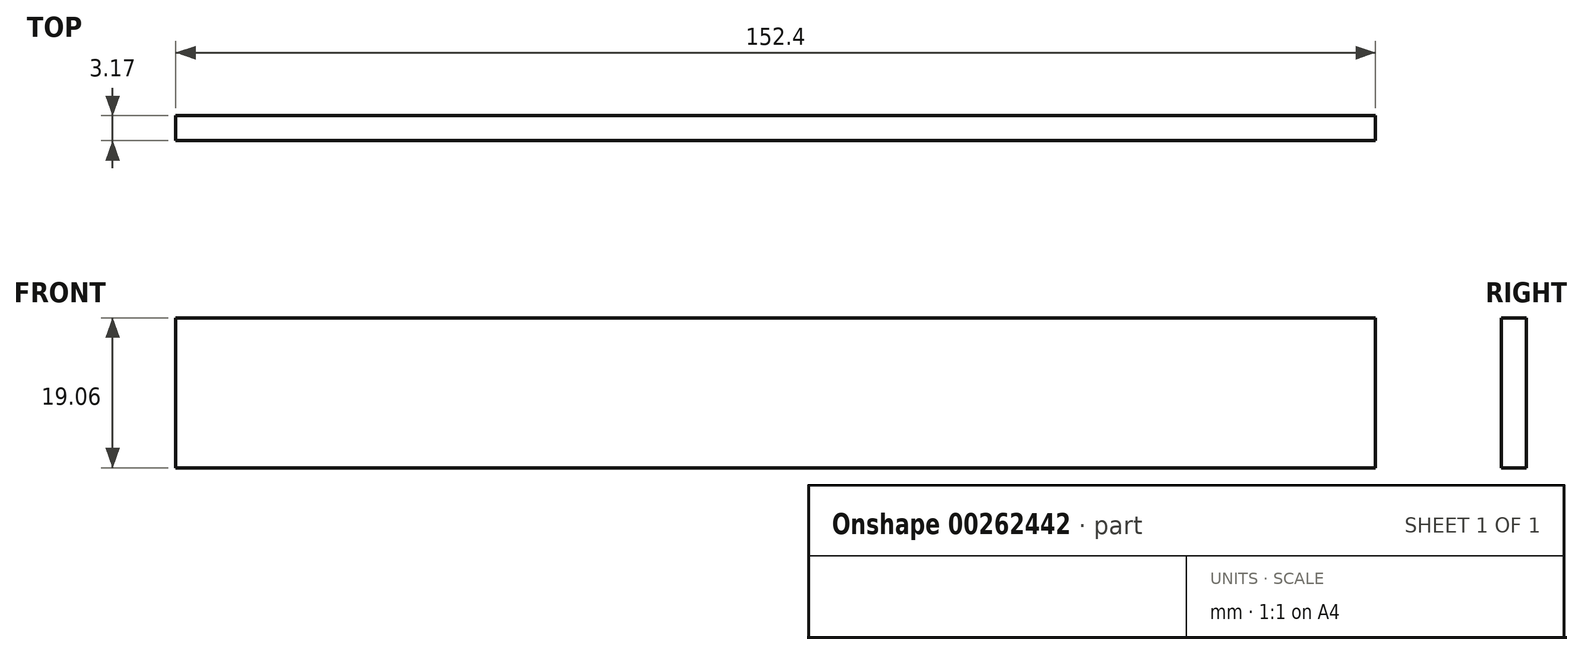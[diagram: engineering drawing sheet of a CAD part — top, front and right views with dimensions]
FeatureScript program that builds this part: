
annotation { "Feature Type Name" : "Feature", "Feature Type Description" : "" }
export const myFeature = defineFeature(function(context is Context, id is Id, definition is map)
    precondition{}
    {
        {
            var Q0;
            Q0=qCreatedBy(makeId("Front.planeOp"),FACE);
            var sketch = newSketch(context, id + "F0", { "sketchPlane" : qUnion([Q0])});
            skLineSegment(sketch, "E0.bottom", {"start": v(76.2, 9.53) * mm, "end": v(-76.2, 9.53) * mm});
            skLineSegment(sketch, "E0.top", {"start": v(76.2, -9.53) * mm, "end": v(-76.2, -9.53) * mm});
            skLineSegment(sketch, "E0.left", {"start": v(76.2, 9.53) * mm, "end": v(76.2, -9.53) * mm});
            skLineSegment(sketch, "E0.right", {"start": v(-76.2, 9.53) * mm, "end": v(-76.2, -9.53) * mm});
            skPoint(sketch, "E0.middle", {"position": v(0, 0) * mm});
            skSolve(sketch);
        }
        {
            var Q0;
            Q0 = qSketchRegion(id + "F0", true);
            extrude(context, id + "F1", {"entities" : qUnion([Q0]), "depth" : 3.17 * mm});
        }
    });
